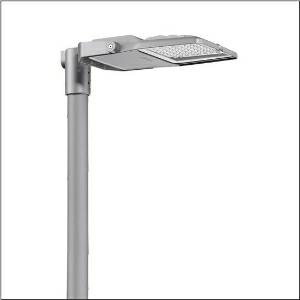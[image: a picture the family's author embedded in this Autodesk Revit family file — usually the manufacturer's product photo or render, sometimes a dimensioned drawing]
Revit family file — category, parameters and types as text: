
# Revit family: floodlight_fl_21_iq_mini___pl61_5xa7771d2c3a_41a8
name_source: partatom
category: Lighting Fixtures
units: mm (PartAtom-declared; Revit-internal decimal feet)

## family parameters
Cut with Voids When Loaded = No
Host = Face
Light Source = No
Part Type = Normal
Room Calculation Point = No
Round Connector Dimension = Use Diameter
Shared = No

## types (1)
- --- (1 x LED, 17500 lm, 143 W, 3000K)
    Apparent Load = 143 VA
    CIE Flux Codes = 33 65 98 100 100
    Color Rendering = 70
    Color Temperature = 3000K
    Default Elevation = 1800 mm
    Description = Floodlight FL 21 iQ mini, floodlight, primary light control with lens, of PMMA, primary optical cover: protective disc, of toughened safety glass, transparent, light distribution: PL61, light emission: direct distribution, installation type: surface-mounted, lamps: LED, High Power LED, rated values: 17.500lm | 143W | 122,4lm/W (begin service life); end service life: 17.500lm | 151,6W; at 50% lumin. flux: 8.750lm | 60,6W | 144,4lm/W, colour temperature: 3000K, colour rendering: CRI > 70, light colour: 730, light setting 1 begin service life: 100% | 17.500lm | 143W | 122,4lm/W | 3.000K, light setting 1 end service life: 151,6W, further light settings possible, control: Auto-Match, Temp-Guard, Lumen-Switch, Night-Set, Smart-Wire, Light-Fading, Desk-Remote (wireless, voltage-free reading and setting of iQ features in the workshop via application-optimized NFC function/RFID function), optimised constant luminous flux control (CLO 2.0), pre-setting: linear dimming characteristic, with terminal, 6-pole, mains connection: 220..240V, AC, 50/60Hz, luminaire housing, of diecast aluminium, powder-coated, SITECO metallic grey (DB 702S), corrosivity category C5 mid according to DIN EN ISO 12944suitable for swimming poolschlorine-resistant, sealing non-destructively replaceable, please order mast flange separately, mast bracket, of steel, galvanised, powder-coated, SITECO metallic grey (DB 702S), protection rating (complete): IP66, insulation class (complete): insulation class II (safety insulation), certification: CE, ENEC, VDE, protection symbol: D, impact resistance: IK08, permissible operating ambient temperature: -40..+40°C, permissible operating ambient temperature for outdoor applications: -40..+50°C, standard: DIN EN 12944, LABS conformity tested according to VDMA 24364:2018-05, packaging unit: 1 piece

Light Distribution: PL61
    Height = 70 mm
    Lamp = 1 x LED
    Lamp Light Flux = 17500 lm
    Lamp Power = 143 W
    Lamp count = 1
    Length = 485 mm
    Luminous efficacy = 122 lm/W
    Manufacturer = Siteco
    ModVariant = No
    Model = 5XA7771D2C3A
    Number of Poles = 1
    OnlyDefault = Yes
    Power Factor = 1
    Product Name = Floodlight FL 21 iQ mini | PL61
    Product group = floodlight | pylon annexe
    ProductGroupID = 6201
    Protection Class = Protection class II
    Protection Degree = IP 66
    RLX_Detail_Level = 1
    RLX_Emergency_Light_Flux = 0 lm
    RLX_Emergency_Type = 0
    RLX_Emergency_Type_DB = No
    RlxData = <blob elided: 101909 chars, md5=bce95795>
    Socket = socket
    Standby Power = 0 W
    System Light Flux = 17500 lm
    System Power = 143 W
    Type Comments = factory setting: luminous flux: 100 % | dim-lin: 254 | 730 mA
    Type Image = l_1007125.jpg
    URL = http://relux.com
    VarID = @adj_172203
    Voltage = 0 V
    Weight = 0.00 kg
    Width = 337 mm

## geometry (parser evidence)
native form markers: Blend x4, Sweep x11
no freeform markers — native parametric forms only
